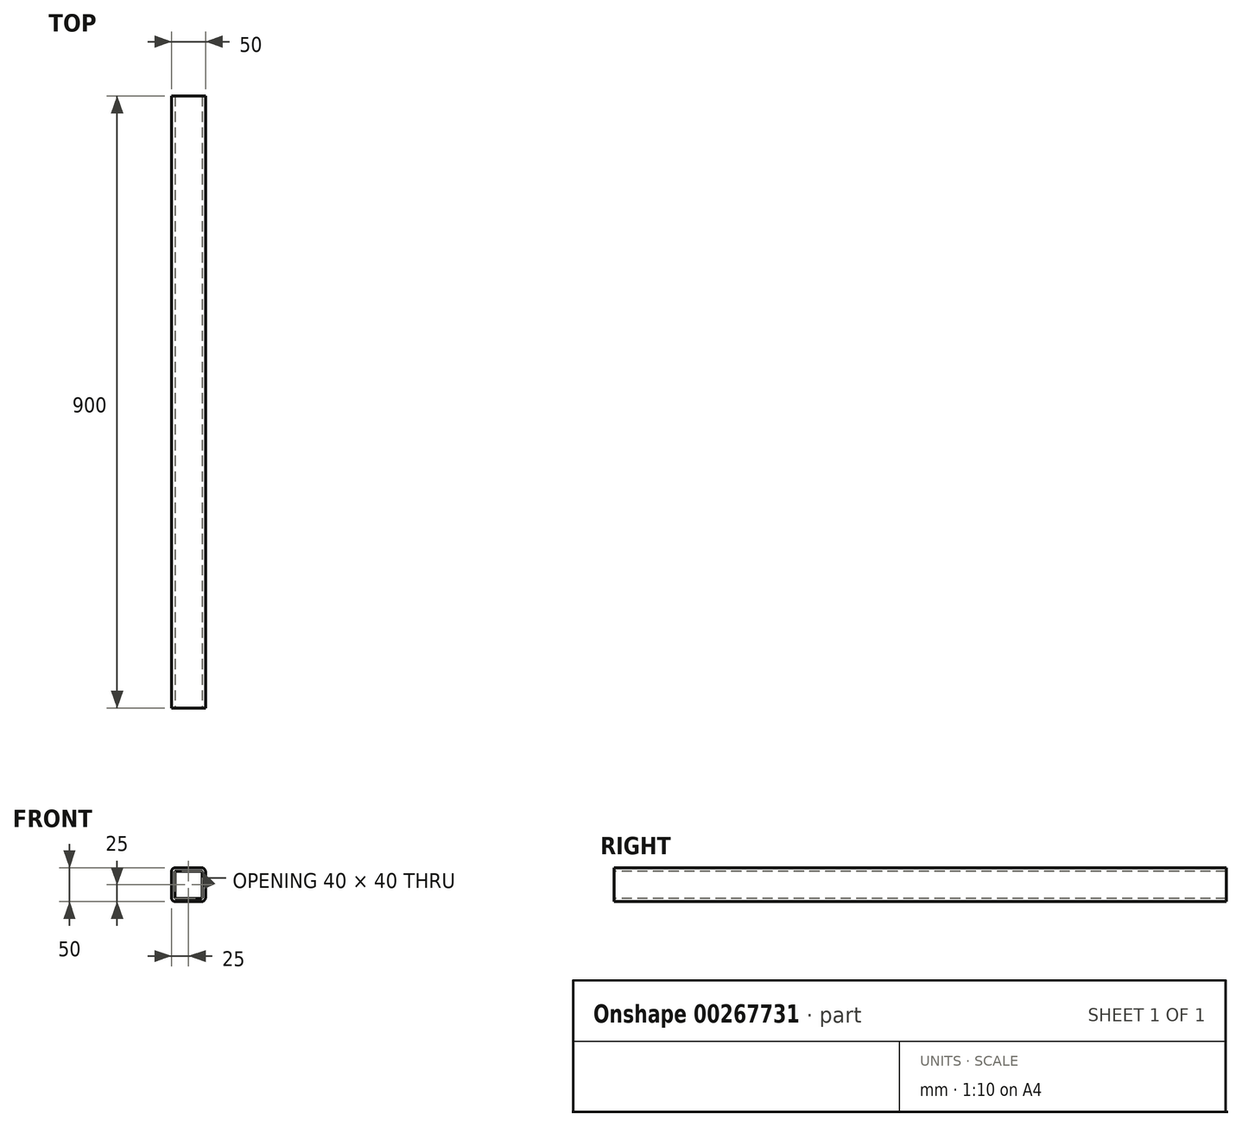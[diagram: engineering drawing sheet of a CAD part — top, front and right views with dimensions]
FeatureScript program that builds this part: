
annotation { "Feature Type Name" : "Feature", "Feature Type Description" : "" }
export const myFeature = defineFeature(function(context is Context, id is Id, definition is map)
    precondition{}
    {
        {
            var Q0;
            Q0=qCreatedBy(makeId("Front.planeOp"),FACE);
            var sketch = newSketch(context, id + "F0", { "sketchPlane" : qUnion([Q0])});
            skLineSegment(sketch, "E0.bottom", {"start": v(19, -25) * mm, "end": v(-19, -25) * mm});
            skLineSegment(sketch, "E0.top", {"start": v(19, 25) * mm, "end": v(-19, 25) * mm});
            skLineSegment(sketch, "E0.left", {"start": v(25, -19) * mm, "end": v(25, 19) * mm});
            skLineSegment(sketch, "E0.right", {"start": v(-25, -19) * mm, "end": v(-25, 19) * mm});
            skPoint(sketch, "E0.middle", {"position": v(0, 0) * mm});
            skPoint(sketch, "E1.visualSharp", {"position": v(-25, 25) * mm});
            skArc(sketch, "E1.filletArc", {"start": v(-19, 25) * mm, "mid": v(-23.24, 23.24) * mm, "end": v(-25, 19) * mm});
            skPoint(sketch, "E2.visualSharp", {"position": v(25, 25) * mm});
            skArc(sketch, "E2.filletArc", {"start": v(25, 19) * mm, "mid": v(23.24, 23.24) * mm, "end": v(19, 25) * mm});
            skPoint(sketch, "E3.visualSharp", {"position": v(25, -25) * mm});
            skArc(sketch, "E3.filletArc", {"start": v(19, -25) * mm, "mid": v(23.24, -23.24) * mm, "end": v(25, -19) * mm});
            skPoint(sketch, "E4.visualSharp", {"position": v(-25, -25) * mm});
            skArc(sketch, "E4.filletArc", {"start": v(-25, -19) * mm, "mid": v(-23.24, -23.24) * mm, "end": v(-19, -25) * mm});
            skArc(sketch, "E5.0", {"start": v(-20, -19) * mm, "mid": v(-19.7, -19.7) * mm, "end": v(-19, -20) * mm});
            skLineSegment(sketch, "E5.1", {"start": v(19, -20) * mm, "end": v(-19, -20) * mm});
            skLineSegment(sketch, "E5.2", {"start": v(-20, -19) * mm, "end": v(-20, 19) * mm});
            skArc(sketch, "E5.3", {"start": v(19, -20) * mm, "mid": v(19.7, -19.7) * mm, "end": v(20, -19) * mm});
            skArc(sketch, "E5.4", {"start": v(-19, 20) * mm, "mid": v(-19.7, 19.7) * mm, "end": v(-20, 19) * mm});
            skLineSegment(sketch, "E5.5", {"start": v(19, 20) * mm, "end": v(-19, 20) * mm});
            skArc(sketch, "E5.6", {"start": v(20, 19) * mm, "mid": v(19.7, 19.7) * mm, "end": v(19, 20) * mm});
            skLineSegment(sketch, "E5.7", {"start": v(20, -19) * mm, "end": v(20, 19) * mm});
            skSolve(sketch);
        }
        {
            var Q0;
            Q0=qSketchRegion(id+"F0",true);
            extrude(context, id + "F1", {"entities" : qUnion([Q0]), "oppositeDirection" : true, "depth" : 900 * mm});
        }
    });
